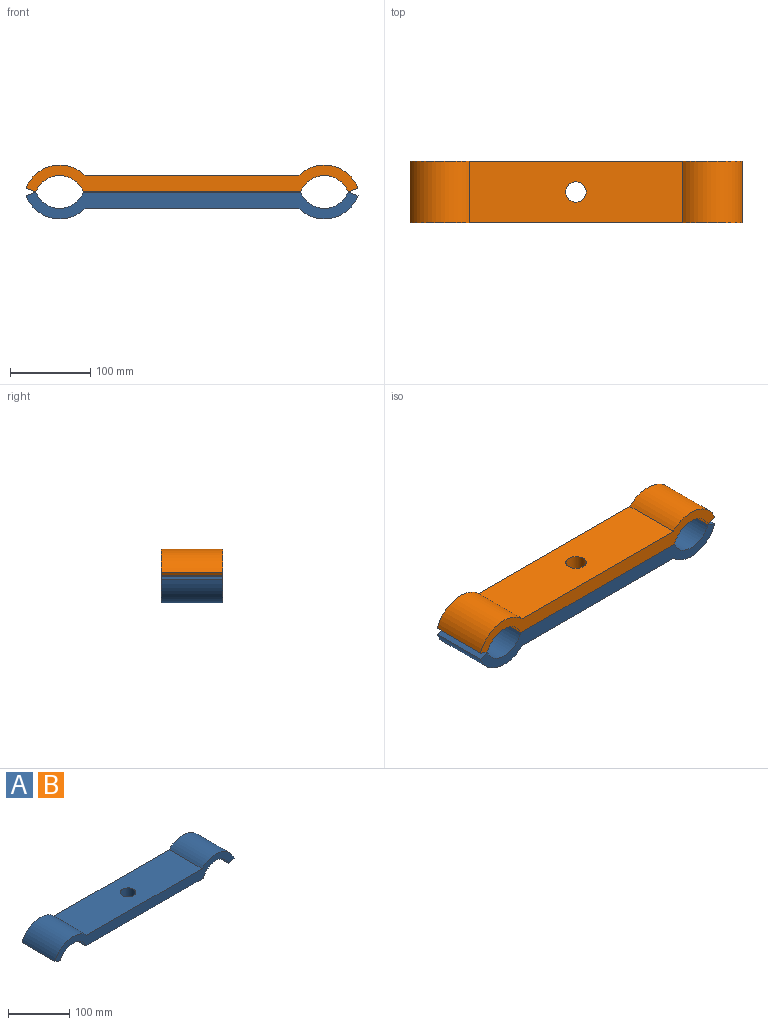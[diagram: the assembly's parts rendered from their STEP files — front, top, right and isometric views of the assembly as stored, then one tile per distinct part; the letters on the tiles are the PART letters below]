
ASSEMBLY  parts=2 mates=1
PART A: 11 faces, bbox 414.2x76.2x33.7 mm
  f0: plane 270.8x76.2mm, normal (0,0,-1), area 20128.3mm2, adj f1,f7,f8,f9,f10
  f1: cylinder r=31.75mm len=76.2mm, axis (0,1,0), area 5852.1mm2, adj f0,f2,f8,f9
  f2: plane 76.2x12.3mm, normal (0.35,0,-0.94), area 1002.1mm2, adj f1,f3,f8,f9
  f3: cylinder r=44.9mm len=76.2mm, axis (0,1,0), area 6825.3mm2, adj f2,f4,f8,f9
  f4: plane 266.7x76.2mm, normal (0,0,1), area 19815.8mm2, adj f3,f5,f8,f9,f10
  f5: cylinder r=44.9mm len=76.2mm, axis (0,1,0), area 6825.3mm2, adj f4,f6,f8,f9
  f6: plane 76.2x12.3mm, normal (-0.35,0,-0.94), area 1002.1mm2, adj f5,f7,f8,f9
  f7: cylinder r=31.75mm len=76.2mm, axis (0,1,0), area 5852.1mm2, adj f0,f6,f8,f9
  f8: plane 414.2x33.68mm, normal (0,-1,0), area 7686mm2, adj f0,f1,f2,f3,f4,f5,f6,f7
  f9: plane 414.2x33.68mm, normal (0,1,0), area 7686mm2, adj f0,f1,f2,f3,f4,f5,f6,f7
  f10: cylinder r=12.7mm len=25.4mm, axis (0,0,1), area 1637.8mm2, adj f0,f4
PART B: same geometry as A
PLACE A rot(axis=(1,0,0),180deg) t=(-58.97,103.24,178.82)mm
PLACE B t=(-58.97,179.44,188.12)mm
MATE fastened A.f10 <-> B.f10  axis (0,0,1) through (-58.97,141.34,183.47)mm
